# Revit family: Lighting-UrbanLighting-GEWISS-ELIA-BL-LED_POLE_700mm
name_source: partatom
category: Apparecchi per illuminazione
units: mm (PartAtom-declared; Revit-internal decimal feet)

## family parameters
Condiviso = No
Host = Superficie
Punto di calcolo locali = Sì
Quota connettore circolare = Usa diametro
Sorgente d'illuminazione = Sì
Taglio con vuoti quando caricato = No
Tipo di parte = Normale

## types (3) — shared parameters
Angolo campo riflettore = 90.00°
Angolo inclinazione = 90.00°
Angolo raggio riflettore = 30.00°
Application = External
Body = Die-cast aluminium -
Catalogue = LIGHTING
Classification: = -
Color Rendering Index = CRI>80
Colour = Black
Colour : = -
Context = Outdoor architectural lighting
Control System = Stand alone
DIN 18032-3 certification = -
Device with reduced surface temperature = -
Driver = Included
Driver Box = Built-in
Driver failure rate = F025 = 50.000h Tq 25°C
Electrocod = 2419
Eletrical and lighting features = -
Emetti da diametro cerchio = 100 mm  [stored 0.328084 ft]
External screw = -
Filtro dei colori = 16777215
Fixing = Stainless steel support
Gasket = -
General information = -
Glow Wire Test : = 750 °C
IDF = 72b3dd12-8640-468c-82a6-6aef94e46311
IDT = 2f89f132-1269-468a-bfb5-5e1ea4b97a78
IP degree = IP65
IPEA = -
Immagine tipo = EliaBL.jpg
Installationa and maintenance = -
Insulation class = I
LED Maintenance = Not available
Lifetime = L80B50 (Tq25°C) = 50.000h
Locking Hook = -
Lugnezza massima = 74 mm  [stored 0.242782 ft]
Luminaire = LED luminaire for diffuse light
Lunghezza simbolo sorgente d'illuminazione = 500 mm  [stored 1.64042 ft]
Materials = -
Maximum surface exposed to the wind : = -
Mouting and installation = Earth
Operating temperature : = -20° +45°
Optic = Wide opal
Optic : = -
Optic Maintenance = Not available
Optic and illuminating features = -
Overvoltage protection = DM 0,5KV / CM 1KV
POSIZIONE = 80000
Photobiological Risk Class = RG0
Produttore = GEWISS S.p.A.
Prospetto di default = 1219 mm
Rated frequency (Hz) = 50/60 Hz
Rendi la forma visibile nel rendering = No
Shield type = Polycarbonate
Shock resistance = IK08
Standard Deviation Colour Matching = SDCM = 5
Standard- = -
Standards and approvals = -
Stocking temperature = -20° +65°
Technical sheet = https://www.gewiss.com
Tilt- = -
Type of light source = LED - Not replaceable
URL = https://www.gewiss.com
Unified Glare Rating = UGR < 25
Unique digital code (Datamatrix) = Currently not present
Variazione temperatura colore lampada con luminosità attenuata = <Nessuno>
Version file RFA = 21.4
Versions = Standard 700 mm
Warranty = 5 years
Wiring = With connection terminal
larghezza lampada = 50 mm  [stored 0.164042 ft]

## per-type parameters (varying)
| type | Descrizione | EAN code | Modello | Supply voltage |
| GWF2300PR857 - ELIA BL ST AL ON/OFF 5700K 700 MM | ELIA BL ST AL ON/OFF 5700K 700 MM | 8034035077418 | GWF2300PR857 |  |
| GWF2300PR840 - ELIA BL ST AL ON/OFF 4000K 700 MM | ELIA BL ST AL ON/OFF 4000K 700 MM | 8034035077401 | GWF2300PR840 |  |
| GWF2300PR830 - ELIA BL ST AL ON/OFF 3000K 700 MM | ELIA BL ST AL ON/OFF 3000K 700 MM | 8034035077548 | GWF2300PR830 | 100-240 V |

note: [stored X ft] marks values corroborated as IEEE doubles in the binary element streams (Revit-internal decimal feet)
